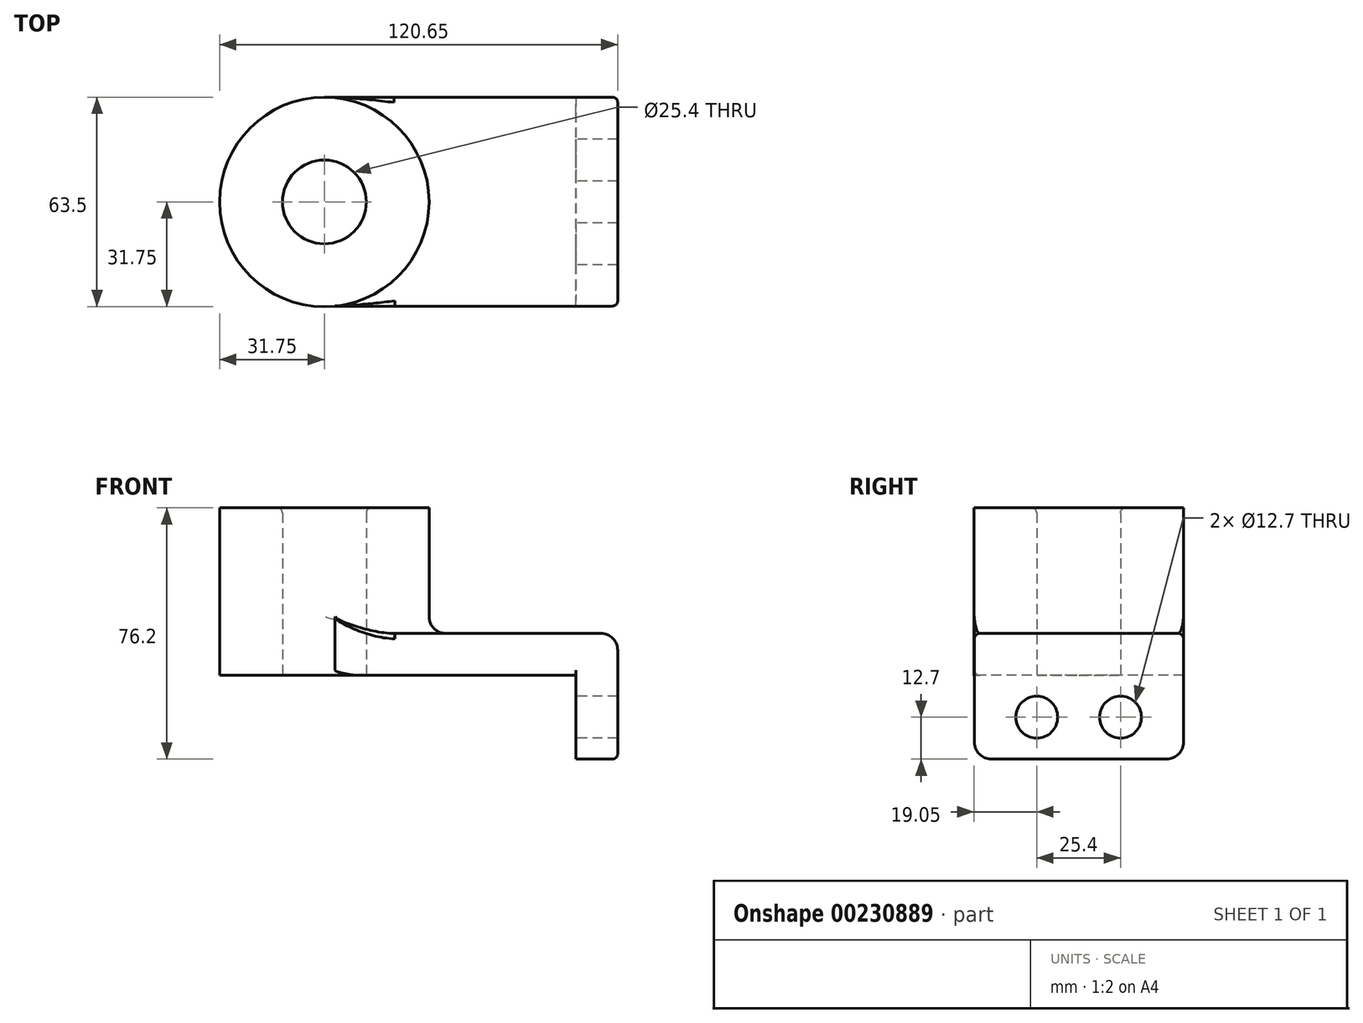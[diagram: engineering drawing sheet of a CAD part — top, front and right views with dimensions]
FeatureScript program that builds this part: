
annotation { "Feature Type Name" : "Feature", "Feature Type Description" : "" }
export const myFeature = defineFeature(function(context is Context, id is Id, definition is map)
    precondition{}
    {
        {
            var Q0;
            Q0=qCreatedBy(makeId("Top.planeOp"),FACE);
            var sketch = newSketch(context, id + "F0", { "sketchPlane" : qUnion([Q0])});
            skCircle(sketch, "E0", {"center": v(0, 0) * mm, "radius": 31.75 * mm});
            skCircle(sketch, "E1", {"center": v(0, 0) * mm, "radius": 12.7 * mm});
            skLineSegment(sketch, "E2.bottom", {"start": v(0, 31.75) * mm, "end": v(76.2, 31.75) * mm});
            skLineSegment(sketch, "E2.top", {"start": v(0, -31.58) * mm, "end": v(76.2, -31.58) * mm});
            skLineSegment(sketch, "E2.left", {"start": v(0, 31.75) * mm, "end": v(0, -31.58) * mm});
            skLineSegment(sketch, "E2.right", {"start": v(76.2, 31.75) * mm, "end": v(76.2, -31.58) * mm});
            skSolve(sketch);
        }
        {
            var Q0;
            Q0 = qSketchRegion(id + "F0", true);
            extrude(context, id + "F1", {"entities" : qUnion([Q0]), "depth" : 12.7 * mm});
        }
        {
            var Q0;
            {var subQ0=sQuery(id+"F0.wireOp",EDGE,"E2.left");var subQ3=sQuery(id+"F0.wireOp",EDGE,"E1");var subQ4=makeQuery(id+"F0.imprint","INTERSECT",VERTEX,{"disambiguationData":[OD(0.0)],"derivedFrom":[subQ3,subQ0]});Q0=makeQuery(id+"F0.imprint","IMPRINT",FACE,{"disambiguationData":[TD([[makeQuery(id+"F0.imprint","IMPRINT",EDGE,{"disambiguationData":[TD([[subQ4,-1.0]])],"derivedFrom":subQ3}),-1.0]])]});}
            var Q1;
            {var subQ0=sQuery(id+"F0.wireOp",EDGE,"E2.left");var subQ3=sQuery(id+"F0.wireOp",EDGE,"E1");var subQ4=makeQuery(id+"F0.imprint","INTERSECT",VERTEX,{"disambiguationData":[OD(0.0)],"derivedFrom":[subQ3,subQ0]});Q1=makeQuery(id+"F0.imprint","IMPRINT",FACE,{"disambiguationData":[TD([[makeQuery(id+"F0.imprint","IMPRINT",EDGE,{"disambiguationData":[TD([[subQ4,1.0]])],"derivedFrom":subQ3}),-1.0]])]});}
            extrude(context, id + "F2", {"entities" : qUnion([Q0, Q1]), "operationType" : NewBodyOperationType.ADD, "depth" : 50.8 * mm});
        }
        {
            var Q0;
            Q0=makeQuery(id+"F1.opExtrude","SWEPT_FACE",FACE,{"disambiguationData":[OSD([sQuery(id+"F0.wireOp",EDGE,"E2.right")])]});
            var sketch = newSketch(context, id + "F3", { "sketchPlane" : qUnion([Q0])});
            skLineSegment(sketch, "E3.bottom", {"start": v(-31.58, 12.7) * mm, "end": v(31.75, 12.7) * mm});
            skLineSegment(sketch, "E3.top", {"start": v(-31.58, -25.4) * mm, "end": v(31.75, -25.4) * mm});
            skLineSegment(sketch, "E3.left", {"start": v(-31.58, 12.7) * mm, "end": v(-31.58, -25.4) * mm});
            skLineSegment(sketch, "E3.right", {"start": v(31.75, 12.7) * mm, "end": v(31.75, -25.4) * mm});
            skCircle(sketch, "E4", {"center": v(-12.7, -12.7) * mm, "radius": 6.35 * mm});
            skLineSegment(sketch, "E5", {"start": v(0, 0) * mm, "end": v(0, -25.4) * mm});
            skCircle(sketch, "E6.MirrorC", {"center": v(12.7, -12.7) * mm, "radius": 6.35 * mm});
            skSolve(sketch);
        }
        {
            var Q0;
            Q0 = qSketchRegion(id + "F3", true);
            extrude(context, id + "F4", {"entities" : qUnion([Q0]), "operationType" : NewBodyOperationType.ADD, "depth" : 12.7 * mm});
        }
        {
            var Q0;
            {var subQ0=sQuery(id+"F0.wireOp",EDGE,"E0");Q0=makeQuery(id+"F2.boolean.opBoolean","INTERSECT",EDGE,{"derivedFrom":[makeQuery(id+"F1.opExtrude","CAP_FACE",FACE,{"disambiguationData":[OSD([subQ0,sQuery(id+"F0.wireOp",EDGE,"E1"),sQuery(id+"F0.wireOp",EDGE,"E2.bottom"),sQuery(id+"F0.wireOp",EDGE,"E2.top"),sQuery(id+"F0.wireOp",EDGE,"E2.right")])],"isStart":false}),makeQuery(id+"F2.opExtrude","SWEPT_FACE",FACE,{"disambiguationData":[OSD([subQ0])]})]});}
            var Q1;
            Q1=makeQuery(id+"F4.opExtrude","CAP_EDGE",EDGE,{"disambiguationData":[OSD([sQuery(id+"F3.wireOp",EDGE,"E3.bottom")])],"isStart":false});
            var Q2;
            Q2=makeQuery(id+"F4.opExtrude","SWEPT_EDGE",EDGE,{"disambiguationData":[OSD([sQuery(id+"F3.wireOp",EDGE,"E3.top"),sQuery(id+"F3.wireOp",EDGE,"E3.left")])]});
            var Q3;
            Q3=makeQuery(id+"F4.opExtrude","SWEPT_EDGE",EDGE,{"disambiguationData":[OSD([sQuery(id+"F3.wireOp",EDGE,"E3.top"),sQuery(id+"F3.wireOp",EDGE,"E3.right")])]});
            fillet(context, id + "F5", {"entities" : qUnion([Q0, Q1, Q2, Q3]), "radius" : 5.08 * mm, "tangentPropagation" : true, "allowEdgeOverflow" : false});
        }
        {
            var Q0;
            Q0=makeQuery(id+"F4.boolean.opBoolean","MERGE",EDGE,{"derivedFrom":[makeQuery(id+"F1.opExtrude","CAP_EDGE",EDGE,{"disambiguationData":[OSD([sQuery(id+"F0.wireOp",EDGE,"E2.top")])],"isStart":false}),makeQuery(id+"F4.opExtrude","SWEPT_EDGE",EDGE,{"disambiguationData":[OSD([sQuery(id+"F3.wireOp",EDGE,"E3.bottom"),sQuery(id+"F3.wireOp",EDGE,"E3.left")])]})]});
            var Q1;
            Q1=makeQuery(id+"F1.opExtrude","CAP_EDGE",EDGE,{"disambiguationData":[OSD([sQuery(id+"F0.wireOp",EDGE,"E2.top")])],"isStart":true});
            var Q2;
            Q2=makeQuery(id+"F1.opExtrude","CAP_EDGE",EDGE,{"disambiguationData":[OSD([sQuery(id+"F0.wireOp",EDGE,"E2.right")])],"isStart":true});
            var Q3;
            Q3=makeQuery(id+"F2.opExtrude","CAP_EDGE",EDGE,{"disambiguationData":[OSD([sQuery(id+"F0.wireOp",EDGE,"E1")])],"isStart":false});
            fillet(context, id + "F6", {"entities" : qUnion([Q0, Q1, Q2, Q3]), "radius" : 1.59 * mm, "tangentPropagation" : true, "allowEdgeOverflow" : false});
        }
    });
